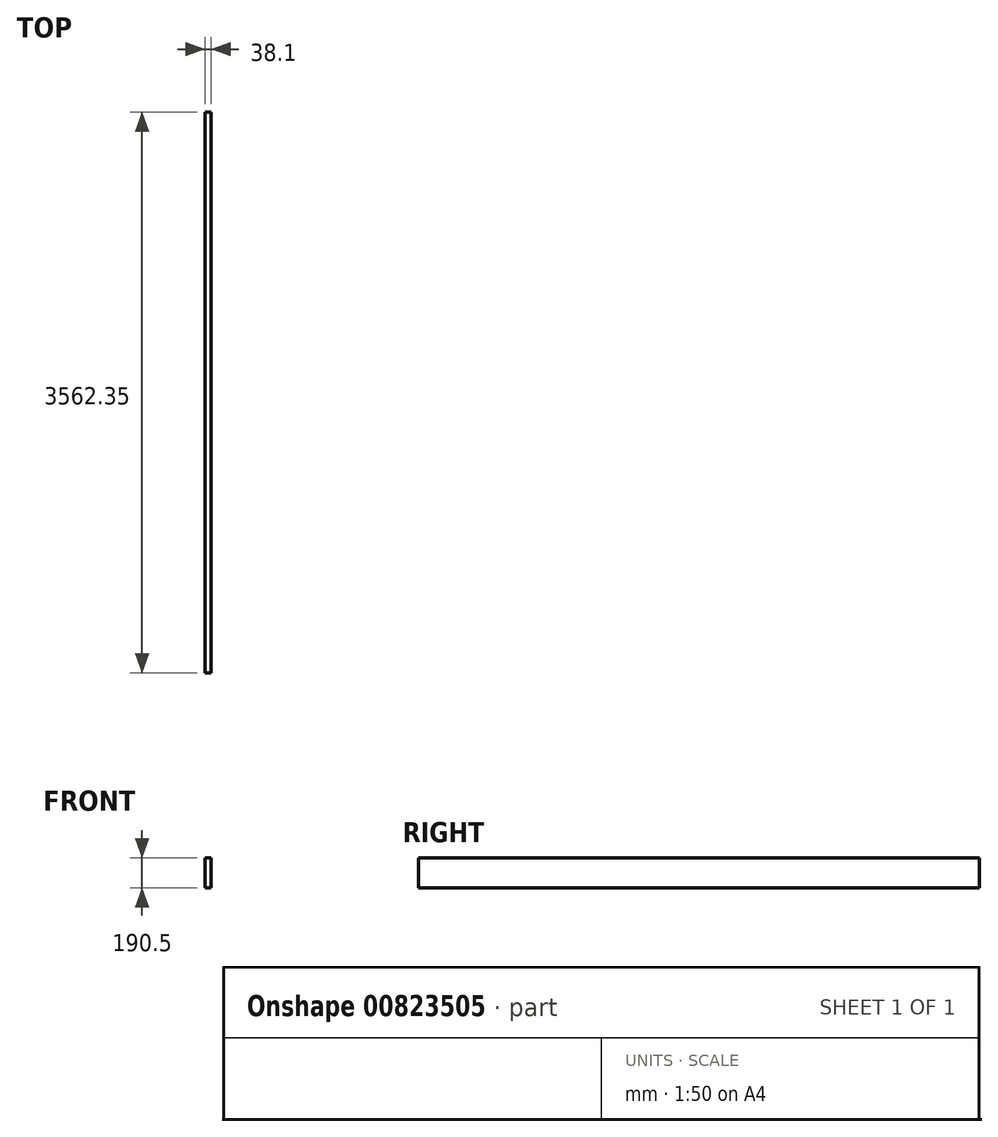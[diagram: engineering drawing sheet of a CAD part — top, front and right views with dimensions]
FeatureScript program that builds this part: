
annotation { "Feature Type Name" : "Feature", "Feature Type Description" : "" }
export const myFeature = defineFeature(function(context is Context, id is Id, definition is map)
    precondition{}
    {
        {
            var Q0;
            Q0=qCreatedBy(makeId("Front.planeOp"),FACE);
            var sketch = newSketch(context, id + "F0", { "sketchPlane" : qUnion([Q0])});
            skLineSegment(sketch, "E0.bottom", {"start": v(0, 0) * mm, "end": v(38.1, 0) * mm});
            skLineSegment(sketch, "E0.top", {"start": v(0, 190.5) * mm, "end": v(38.1, 190.5) * mm});
            skLineSegment(sketch, "E0.left", {"start": v(0, 0) * mm, "end": v(0, 190.5) * mm});
            skLineSegment(sketch, "E0.right", {"start": v(38.1, 0) * mm, "end": v(38.1, 190.5) * mm});
            skSolve(sketch);
        }
        {
            var Q0;
            Q0=qSketchRegion(id+"F0",true);
            extrude(context, id + "F1", {"entities" : qUnion([Q0]), "depth" : 3562.35 * mm, "offsetDistance" : 25.4 * mm});
        }
    });
